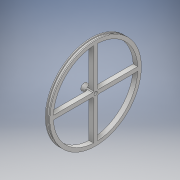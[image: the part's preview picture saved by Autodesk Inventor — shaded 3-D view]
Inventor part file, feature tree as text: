
AUTODESK INVENTOR PART (.ipt)
format: ipt  version: 2018 (Build 220112000, 112)  size: 199,168 bytes
history: native  units: mm
features: extrude x11, sketch x11, pattern_circular x1, fillet x1
ambient origin geometry x8: Origin, YZ Plane, XZ Plane, XY Plane, X Axis, Y Axis, Z Axis, Center Point
bodies: Solid1 (feature_tree)
feature tree (24):
  extrude  "Extrusion1"  Depth=3.5mm TaperAngle=0.0deg
  extrude  "Extrusion2"  Depth=1.0mm TaperAngle=0.0deg
  extrude  "Extrusion3"  Depth=1.0mm TaperAngle=0.0deg
  extrude  "Extrusion4"  Depth=6.0mm TaperAngle=0.0deg
  extrude  "Extrusion5"  Depth=10.0mm TaperAngle=0.0deg
  extrude  "Extrusion6"  Depth=1.0mm TaperAngle=0.0deg
  extrude  "Extrusion7"  Depth=1.0mm
  extrude  "Extrusion8"  Depth=4.0mm
  extrude  "Extrusion9"  Depth=40.0mm TaperAngle=360.0deg
  extrude  "Extrusion10"  Depth=2.0mm TaperAngle=0.0deg
  pattern_circular  "Circular Pattern1"  [2 undecoded]
  fillet  "Fillet1"  [1 undecoded]
  extrude  "Extrusion11"  [1 undecoded]
  sketch  "Sketch1"  dims[d0=88.0mm d1=3.5mm d2=0.0mm]
  sketch  "Sketch2"  dims[d3=90.0mm d4=1.0mm d5=0.0mm]
  sketch  "Sketch3"  dims[d6=90.0mm d7=1.0mm d8=0.0mm]
  sketch  "Sketch4"  dims[d9=83.0mm d10=6.0mm d11=0.0mm]
  sketch  "Sketch5"  dims[d12=7.0mm d13=10.0mm d14=0.0mm]
  sketch  "Sketch6"  dims[d15=2.0mm d16=0.0mm d17=1.0mm d18=0.0mm]
  sketch  "Sketch7"  dims[d19=1.0mm d20=0.0mm d21=3.25mm]
  sketch  "Sketch8"  dims[d22=10.0mm d23=0.0mm d24=4.0mm]
  sketch  "Sketch9"  dims[d25=4.5mm d26=0.0mm d27=40.0mm d28=360.0deg]
  sketch  "Sketch10"  dims[d30=2.0mm d31=2.0mm d32=0.0mm]
  sketch  "Sketch11"
note: 4 required parameter values undecoded (feature->parameter linkage not recoverable at this tier; creation-order binding heuristic only, values carry confidence <= 0.55)
